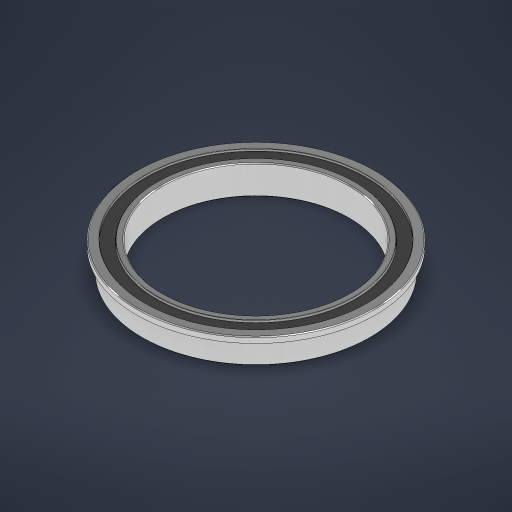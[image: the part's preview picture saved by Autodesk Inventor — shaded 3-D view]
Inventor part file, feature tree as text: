
AUTODESK INVENTOR PART (.ipt)
format: ipt  version: 2024 (Build 280153000, 153)  size: 276,480 bytes
history: native  units: in
note: dims shown in document units (in); Inventor stores cm internally (conversion verified against a paired STEP export)
features: chamfer x1
ambient origin geometry x8: Origin, YZ Plane, XZ Plane, XY Plane, X Axis, Y Axis, Z Axis, Center Point
bodies: Solid1 (feature_tree)
feature tree (1):
  chamfer  "Chamfer3"  [1 undecoded]
note: 1 required parameter value undecoded (feature->parameter linkage not recoverable at this tier; creation-order binding heuristic only, values carry confidence <= 0.55)
